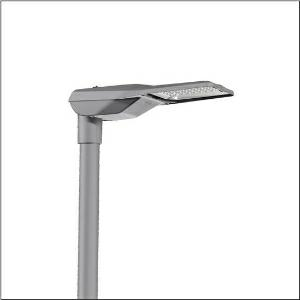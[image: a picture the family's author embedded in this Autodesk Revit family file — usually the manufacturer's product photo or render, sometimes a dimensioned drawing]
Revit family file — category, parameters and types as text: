
# Revit family: streetlight_sl_21_mini___p0_5a_5xe2v33s08hb_986b
name_source: partatom
category: Lighting Fixtures
units: mm (PartAtom-declared; Revit-internal decimal feet)

## family parameters
Cut with Voids When Loaded = No
Host = Face
Light Source = No
Part Type = Normal
Room Calculation Point = No
Round Connector Dimension = Use Diameter
Shared = No

## types (1)
- --- (1 x LED, 8890 lm, 66 W, 3000K)
    Apparent Load = 66 VA
    CIE Flux Codes = 37 73 96 100 100
    Color Rendering = 70
    Color Temperature = 3000K
    Default Elevation = 1800 mm
    Description = Streetlight SL 21 mini, mast luminaire, primary light control with lens, of PMMA, primary optical cover: cover, of toughened safety glass, transparent, light distribution: P0.5a, light emission: direct distribution, primary light characteristic: asymmetric, installation type: post-top, side-entry, LED, High Power LED, rated luminous flux: 8.890lm, luminous efficacy: 135lm/W, light colour: 730, colour temperature: 3000K, control gear: D4i, control: pre-setting: logarithmic dimming characteristic, flexible luminous flux parameterisation, time-dependent luminous flux control, constant luminous flux control, overheat protection, mains connection: 220..240V, AC, 50/60Hz, start of lifetime: 66W, end of service life: 69W, reduction: 30W, luminaire housing, of diecast aluminium, powder-coated, Siteco® metallic grey (DB 702S), corrosivity category C5 mid according to DIN EN ISO 12944, multi-level sealing system, sealing non-destructively replaceable, inclination adjustable: 0°, 5°, 10°, 15°, please order mast flange separately, length: 628mm, width: 235mm, height: 110mm, mast flange for spigot size: 42mm (side-entry): 5XC10008XM4, 60/48mm (side-entry/post-top): 5XC10108XM2, 76/60mm (side-entry/post-top): 5XC10108XM1, mounting height: 4..8m, Smart Interface above, protection rating (complete): IP66, insulation class (complete): insulation class II (safety insulation), certification: CE, ENEC, ENEC+, VDE, impact resistance: IK10, permissible operating ambient temperature for outdoor applications: -40..+50°C, standard-compliant lighting for roads and squares, packaging unit: 1 piece

Light Distribution: P0.5a
    Height = 110 mm
    Lamp = 1 x LED
    Lamp Light Flux = 8890 lm
    Lamp Power = 66 W
    Lamp count = 1
    Length = 625 mm
    Luminous efficacy = 135 lm/W
    Manufacturer = Siteco
    ModVariant = No
    Model = 5XE2V33S08HB
    Number of Poles = 1
    OnlyDefault = Yes
    Power Factor = 1
    Product Name = Streetlight SL 21 mini | P0.5a
    Product group = mast luminaire | pylon top
    ProductGroupID = 6100
    Protection Class = Protection class II
    Protection Degree = IP 66
    RLX_Detail_Level = 1
    RLX_Emergency_Light_Flux = 0 lm
    RLX_Emergency_Type = 0
    RLX_Emergency_Type_DB = No
    RlxData = <blob elided: 25605 chars, md5=3687c342>
    Socket = socket
    Standby Power = 0 W
    System Light Flux = 8890 lm
    System Power = 66 W
    Type Comments = factory setting: luminous flux: 100 % | dim-lin: 254 | 670 mA
    Type Image = l_1003515.jpg
    URL = http://relux.com
    VarID = @adj_069804
    Voltage = 0 V
    Weight = 0.00 kg
    Width = 234 mm

## geometry (parser evidence)
native form markers: Blend x4, Sweep x11
no freeform markers — native parametric forms only
